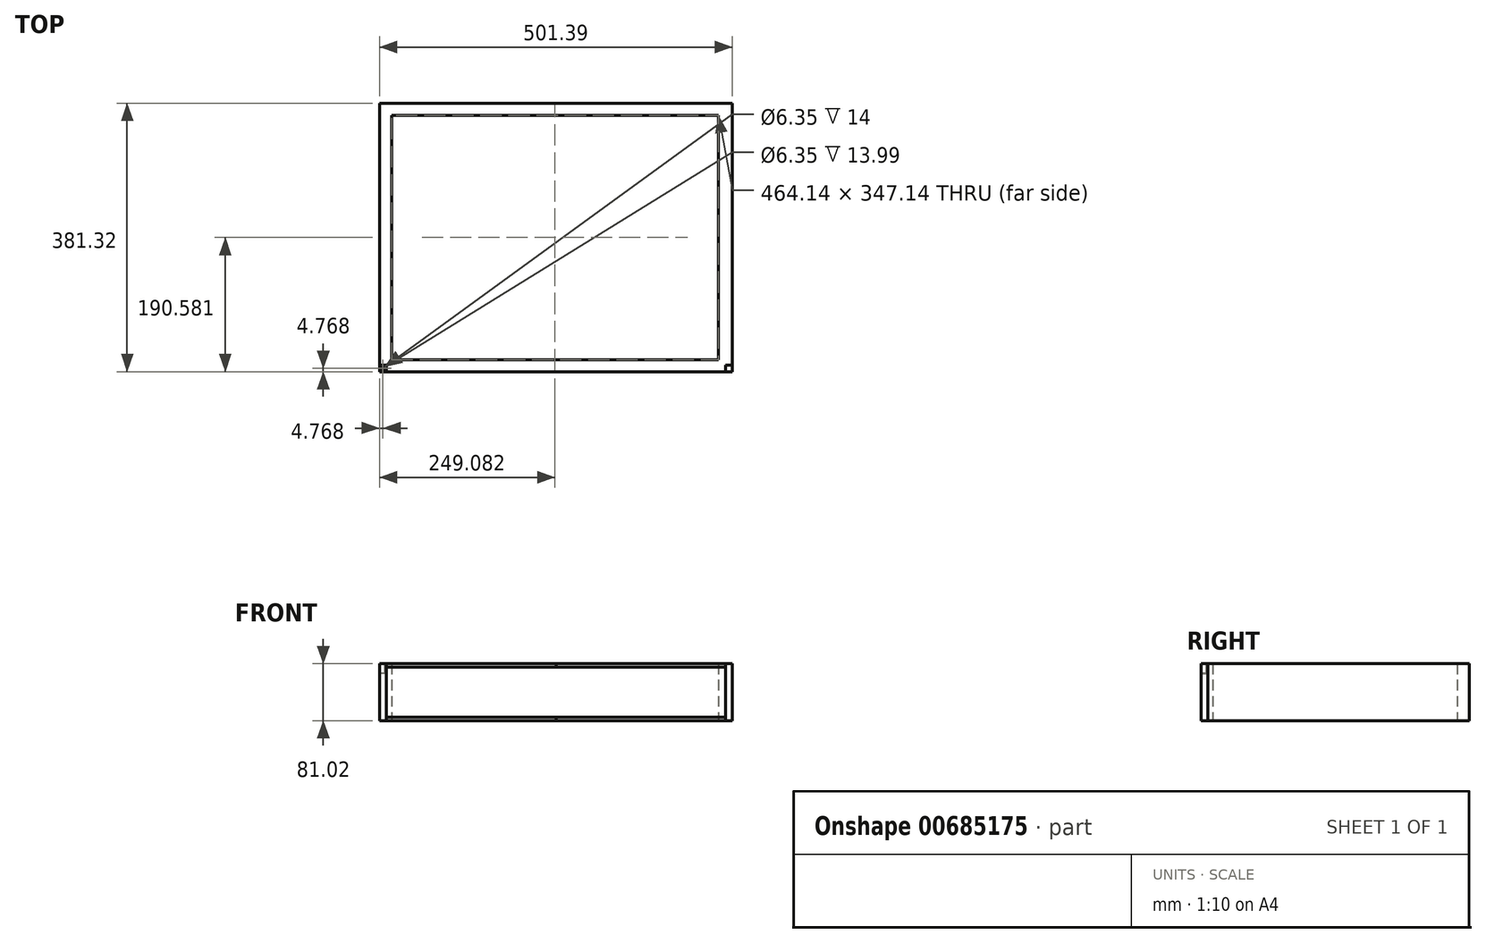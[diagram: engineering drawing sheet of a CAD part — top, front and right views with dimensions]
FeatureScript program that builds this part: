
annotation { "Feature Type Name" : "Feature", "Feature Type Description" : "" }
export const myFeature = defineFeature(function(context is Context, id is Id, definition is map)
    precondition{}
    {
        {
            var Q0;
            Q0=qCreatedBy(makeId("Top.planeOp"),FACE);
            var sketch = newSketch(context, id + "F0", { "sketchPlane" : qUnion([Q0])});
            skLineSegment(sketch, "E0.bottom", {"start": v(0, 0) * mm, "end": v(501.37, 0) * mm});
            skLineSegment(sketch, "E0.top", {"start": v(0, 381.31) * mm, "end": v(501.37, 381.31) * mm});
            skLineSegment(sketch, "E0.left", {"start": v(0, 0) * mm, "end": v(0, 381.31) * mm});
            skLineSegment(sketch, "E0.right", {"start": v(501.37, 0) * mm, "end": v(501.37, 381.31) * mm});
            skLineSegment(sketch, "E1.bottom", {"start": v(17, 17) * mm, "end": v(481.14, 17) * mm});
            skLineSegment(sketch, "E1.top", {"start": v(17, 364.14) * mm, "end": v(481.14, 364.14) * mm});
            skLineSegment(sketch, "E1.left", {"start": v(17, 17) * mm, "end": v(17, 364.14) * mm});
            skLineSegment(sketch, "E1.right", {"start": v(481.14, 17) * mm, "end": v(481.14, 364.14) * mm});
            skSolve(sketch);
        }
        {
            var Q0;
            Q0 = qSketchRegion(id + "F0", true);
            extrude(context, id + "F1", {"entities" : qUnion([Q0]), "depth" : 81 * mm, "offsetDistance" : 25 * mm});
        }
        {
            var Q0;
            Q0=qCreatedBy(makeId("Top.planeOp"),FACE);
            var sketch = newSketch(context, id + "F2", { "sketchPlane" : qUnion([Q0])});
            skLineSegment(sketch, "E2.bottom", {"start": v(0, -0.01) * mm, "end": v(9.52, 0) * mm});
            skLineSegment(sketch, "E2.top", {"start": v(0, 9.52) * mm, "end": v(9.52, 9.52) * mm});
            skLineSegment(sketch, "E2.left", {"start": v(0, -0.01) * mm, "end": v(0, 9.52) * mm});
            skLineSegment(sketch, "E2.right", {"start": v(9.52, 0) * mm, "end": v(9.52, 9.52) * mm});
            skSolve(sketch);
        }
        {
            var Q0;
            Q0 = qSketchRegion(id + "F2", true);
            extrude(context, id + "F3", {"entities" : qUnion([Q0]), "depth" : 81.01 * mm, "offsetDistance" : 25 * mm, "hasSecondDirection" : true, "secondDirectionOppositeDirection" : true, "secondDirectionDepth" : 0.01 * mm});
        }
        {
            var Q0;
            Q0=makeQuery(id+"F3.opExtrude","SWEPT_FACE",FACE,{"disambiguationData":[OSD([sQuery(id+"F2.wireOp",EDGE,"E2.bottom")])]});
            var sketch = newSketch(context, id + "F4", { "sketchPlane" : qUnion([Q0])});
            skLineSegment(sketch, "E3.0", {"start": v(0, -0.01) * mm, "end": v(9.52, -0.01) * mm});
            skPoint(sketch, "E4.0", {"position": v(250.68, 0) * mm});
            skLineSegment(sketch, "E5.bottom", {"start": v(9.51, -0.01) * mm, "end": v(250.68, -0.01) * mm});
            skLineSegment(sketch, "E5.top", {"start": v(9.51, 4.75) * mm, "end": v(250.68, 4.75) * mm});
            skLineSegment(sketch, "E5.left", {"start": v(9.52, -0.01) * mm, "end": v(9.52, 4.75) * mm});
            skLineSegment(sketch, "E5.right", {"start": v(250.68, -0.01) * mm, "end": v(250.68, 4.75) * mm});
            skSolve(sketch);
        }
        {
            var Q0;
            Q0 = qSketchRegion(id + "F4", true);
            extrude(context, id + "F5", {"entities" : qUnion([Q0]), "oppositeDirection" : true, "depth" : 3 / 406.4 * mm, "offsetDistance" : 25 * mm});
        }
        {
            var Q0;
            Q0=makeQuery(id+"F1.opExtrude","SWEPT_FACE",FACE,{"disambiguationData":[OSD([sQuery(id+"F0.wireOp",EDGE,"E0.bottom")])]});
            var sketch = newSketch(context, id + "F6", { "sketchPlane" : qUnion([Q0])});
            skLineSegment(sketch, "E6", {"start": v(250.68, 81) * mm, "end": v(250.68, 169.32) * mm, "construction": true});
            skLineSegment(sketch, "E7", {"start": v(250.68, 81) * mm, "end": v(250.68, 0) * mm, "construction": true});
            skLineSegment(sketch, "E8", {"start": v(250.68, 40.5) * mm, "end": v(-50.17, 40.5) * mm, "construction": true});
            skSolve(sketch);
        }
        {
            var Q0;
            Q0=sQuery(id+"F6.wireOp",EDGE,"E6");
            cPlane(context, id + "F7", {"entities" : qUnion([Q0]), "cplaneType" : CPlaneType.LINE_ANGLE, "offset" : 25 * mm, "angle" : 0 * degree, "width" : 150 * mm, "height" : 150 * mm});
        }
        {
            var Q0;
            Q0=sQuery(id+"F6.wireOp",EDGE,"E8");
            cPlane(context, id + "F8", {"entities" : qUnion([Q0]), "cplaneType" : CPlaneType.LINE_ANGLE, "offset" : 25 * mm, "angle" : 90 * degree, "width" : 150 * mm, "height" : 150 * mm});
        }
        {
            var Q0;
            Q0=makeQuery(id+"F3.opExtrude","SWEPT_BODY",BODY,{"disambiguationData":[OSD([sQuery(id+"F2.wireOp",EDGE,"E2.bottom"),sQuery(id+"F2.wireOp",EDGE,"E2.top"),sQuery(id+"F2.wireOp",EDGE,"E2.left"),sQuery(id+"F2.wireOp",EDGE,"E2.right")])]});
            var Q1;
            Q1=makeQuery(id+"F5.opExtrude","SWEPT_BODY",BODY,{"disambiguationData":[OSD([sQuery(id+"F4.wireOp",EDGE,"E5.bottom"),sQuery(id+"F4.wireOp",EDGE,"E5.top"),sQuery(id+"F4.wireOp",EDGE,"E5.left"),sQuery(id+"F4.wireOp",EDGE,"E5.right")])]});
            var Q2;
            Q2=qCreatedBy(id+"F7.planeOp",FACE);
            mirror(context, id + "F9", {"entities" : qUnion([Q0, Q1]), "mirrorPlane" : qUnion([Q2])});
        }
        {
            var Q0;
            Q0=makeQuery(id+"F9.opPattern","COPY",BODY,{"derivedFrom":makeQuery(id+"F5.opExtrude","SWEPT_BODY",BODY,{"disambiguationData":[OSD([sQuery(id+"F4.wireOp",EDGE,"E5.bottom"),sQuery(id+"F4.wireOp",EDGE,"E5.top"),sQuery(id+"F4.wireOp",EDGE,"E5.left"),sQuery(id+"F4.wireOp",EDGE,"E5.right")])]}),"instanceName":"1"});
            var Q1;
            Q1=makeQuery(id+"F5.opExtrude","SWEPT_BODY",BODY,{"disambiguationData":[OSD([sQuery(id+"F4.wireOp",EDGE,"E5.bottom"),sQuery(id+"F4.wireOp",EDGE,"E5.top"),sQuery(id+"F4.wireOp",EDGE,"E5.left"),sQuery(id+"F4.wireOp",EDGE,"E5.right")])]});
            var Q2;
            Q2=qCreatedBy(id+"F8.planeOp",FACE);
            mirror(context, id + "F10", {"entities" : qUnion([Q0, Q1]), "mirrorPlane" : qUnion([Q2])});
        }
        {
            var Q0;
            Q0=makeQuery(id+"F3.opExtrude","CAP_FACE",FACE,{"disambiguationData":[OSD([sQuery(id+"F2.wireOp",EDGE,"E2.bottom"),sQuery(id+"F2.wireOp",EDGE,"E2.top"),sQuery(id+"F2.wireOp",EDGE,"E2.left"),sQuery(id+"F2.wireOp",EDGE,"E2.right")])],"isStart":false});
            var sketch = newSketch(context, id + "F11", { "sketchPlane" : qUnion([Q0])});
            skLineSegment(sketch, "E9", {"start": v(9.51, 9.51) * mm, "end": v(0, 0) * mm, "construction": true});
            skCircle(sketch, "E10", {"center": v(4.76, 4.76) * mm, "radius": 3.17 * mm});
            skSolve(sketch);
        }
        {
            var Q0;
            Q0 = qSketchRegion(id + "F11", true);
            extrude(context, id + "F12", {"entities" : qUnion([Q0]), "operationType" : NewBodyOperationType.REMOVE, "oppositeDirection" : true, "depth" : 14 * mm, "offsetDistance" : 25 * mm});
        }
    });
